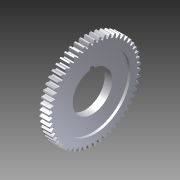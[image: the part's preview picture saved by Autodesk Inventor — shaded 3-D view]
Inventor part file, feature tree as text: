
AUTODESK INVENTOR PART (.ipt)
format: ipt  version: 2012 (Build 160160000, 160)  size: 1,032,192 bytes
history: native  units: in
note: dims shown in document units (in); Inventor stores cm internally (conversion verified against a paired STEP export)
features: sketch x1, extrude x1, imported_body x1
ambient origin geometry x8: Origin, YZ Plane, XZ Plane, XY Plane, X Axis, Y Axis, Z Axis, Center Point
feature tree (3):
  sketch  "Sketch1"  dims[d0=0.375in d3=0.3in d4=0.0in d5=1.0in d6=0.125in d7=0.125in d8=0.0625in d9=0.5625in]
  extrude  "Extrusion2"  Depth=0.3in TaperAngle=0.0deg
  imported_body  "Base1"
